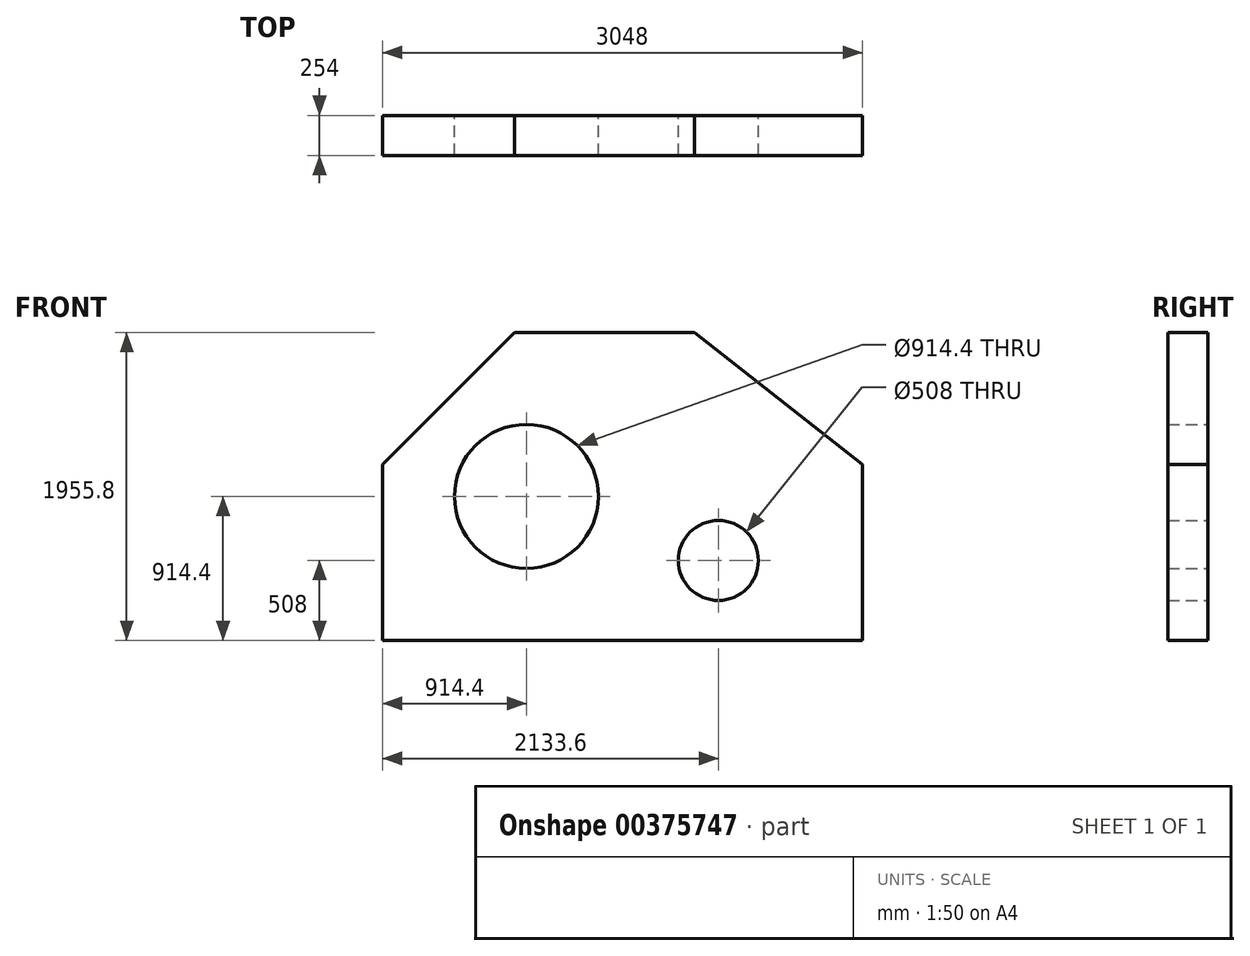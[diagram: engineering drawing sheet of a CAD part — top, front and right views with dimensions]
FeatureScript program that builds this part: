
annotation { "Feature Type Name" : "Feature", "Feature Type Description" : "" }
export const myFeature = defineFeature(function(context is Context, id is Id, definition is map)
    precondition{}
    {
        {
            var Q0;
            Q0=qCreatedBy(makeId("Front.planeOp"),FACE);
            var sketch = newSketch(context, id + "F0", { "sketchPlane" : qUnion([Q0])});
            skLineSegment(sketch, "E0", {"start": v(0, 0) * mm, "end": v(0, -1117.6) * mm});
            skLineSegment(sketch, "E1", {"start": v(0, -1117.6) * mm, "end": v(3048, -1117.6) * mm});
            skLineSegment(sketch, "E2", {"start": v(3048, -1117.6) * mm, "end": v(3048, 0) * mm});
            skLineSegment(sketch, "E3", {"start": v(3048, 0) * mm, "end": v(1981.2, 838.2) * mm});
            skLineSegment(sketch, "E4", {"start": v(1981.2, 838.2) * mm, "end": v(838.2, 838.2) * mm});
            skLineSegment(sketch, "E5", {"start": v(838.2, 838.2) * mm, "end": v(0, 0) * mm});
            skCircle(sketch, "E6", {"center": v(914.4, -203.2) * mm, "radius": 457.2 * mm});
            skCircle(sketch, "E7", {"center": v(2133.6, -609.6) * mm, "radius": 254 * mm});
            skSolve(sketch);
        }
        {
            var Q0;
            Q0=makeQuery(id+"F0.imprint","IMPRINT",FACE,{"disambiguationData":[TD([[makeQuery(id+"F0.imprint","IMPRINT",EDGE,{"derivedFrom":sQuery(id+"F0.wireOp",EDGE,"E0")}),1.0]])]});
            extrude(context, id + "F1", {"entities" : qUnion([Q0]), "depth" : 254 * mm});
        }
    });
